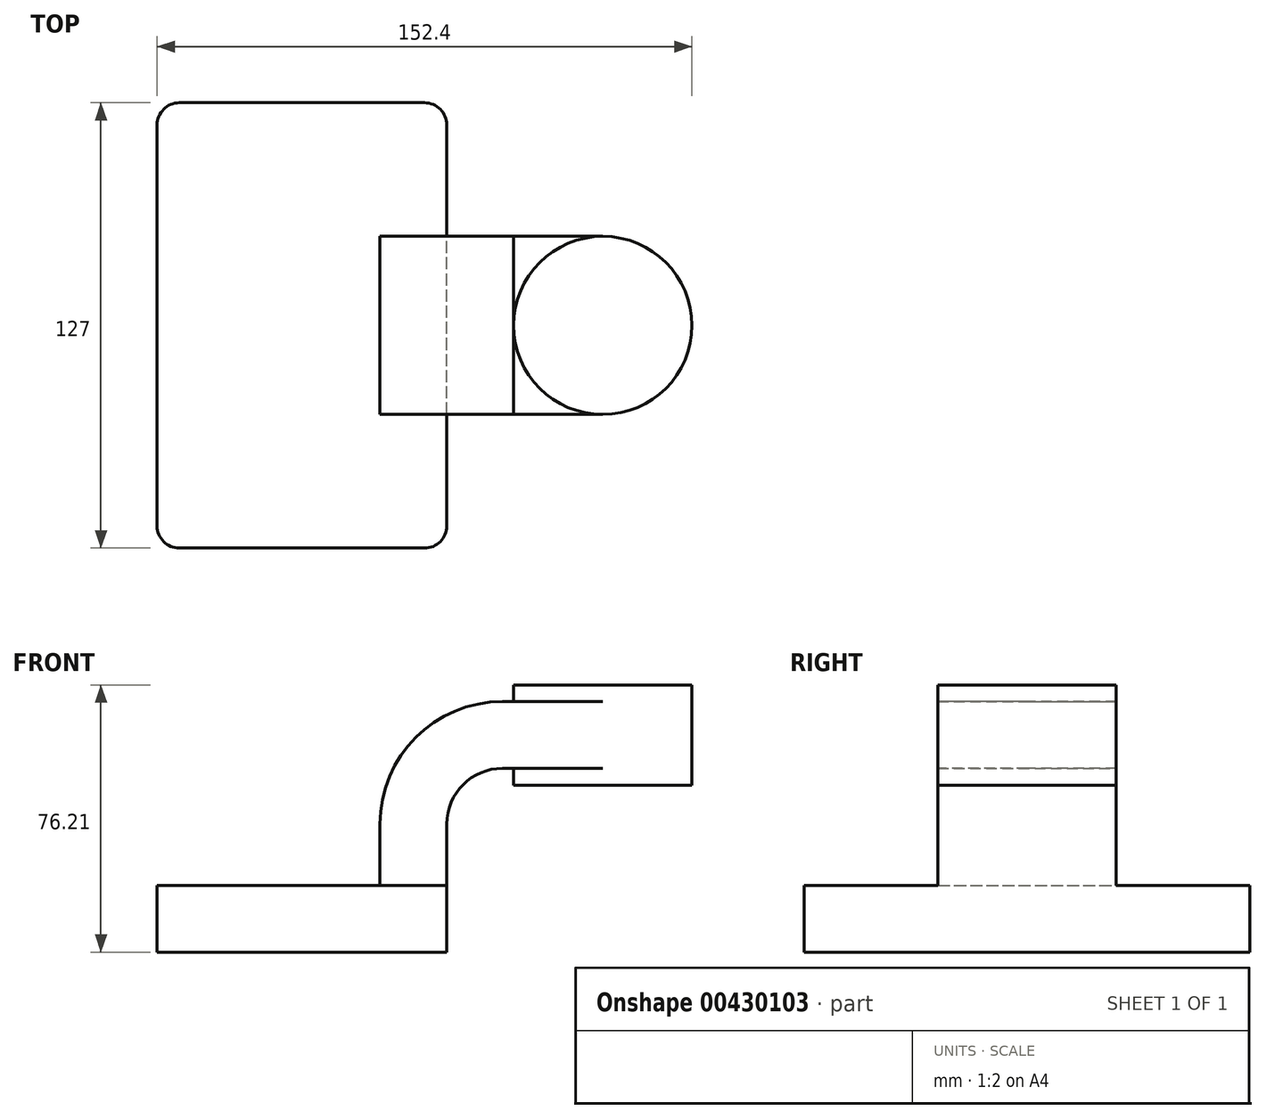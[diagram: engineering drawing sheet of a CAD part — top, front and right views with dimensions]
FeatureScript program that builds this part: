
annotation { "Feature Type Name" : "Feature", "Feature Type Description" : "" }
export const myFeature = defineFeature(function(context is Context, id is Id, definition is map)
    precondition{}
    {
        {
            var Q0;
            Q0=qCreatedBy(makeId("Front.planeOp"),FACE);
            var sketch = newSketch(context, id + "F0", { "sketchPlane" : qUnion([Q0])});
            skLineSegment(sketch, "E0.bottom", {"start": v(-41.28, -9.53) * mm, "end": v(41.28, -9.53) * mm});
            skLineSegment(sketch, "E0.top", {"start": v(-41.28, 9.53) * mm, "end": v(41.28, 9.53) * mm});
            skLineSegment(sketch, "E0.left", {"start": v(-41.28, -9.53) * mm, "end": v(-41.28, 9.53) * mm});
            skLineSegment(sketch, "E0.right", {"start": v(41.28, -9.53) * mm, "end": v(41.28, 9.53) * mm});
            skPoint(sketch, "E0.middle", {"position": v(0, 0) * mm});
            skLineSegment(sketch, "E1.bottom", {"start": v(60.32, 38.1) * mm, "end": v(111.12, 38.1) * mm});
            skLineSegment(sketch, "E1.top", {"start": v(60.32, 66.68) * mm, "end": v(111.12, 66.68) * mm});
            skLineSegment(sketch, "E1.left", {"start": v(60.32, 38.1) * mm, "end": v(60.32, 66.67) * mm});
            skLineSegment(sketch, "E1.right", {"start": v(111.12, 38.1) * mm, "end": v(111.12, 66.67) * mm});
            skPoint(sketch, "E1.middle", {"position": v(85.72, 52.39) * mm});
            skLineSegment(sketch, "E2", {"start": v(41.27, 9.53) * mm, "end": v(41.27, 27) * mm});
            skArc(sketch, "E3", {"start": v(41.27, 27) * mm, "mid": v(45.92, 38.23) * mm, "end": v(57.15, 42.88) * mm});
            skLineSegment(sketch, "E4", {"start": v(57.15, 42.88) * mm, "end": v(85.72, 42.88) * mm});
            skLineSegment(sketch, "E5.0", {"start": v(57.15, 61.93) * mm, "end": v(85.72, 61.93) * mm});
            skArc(sketch, "E5.1", {"start": v(22.22, 27) * mm, "mid": v(32.45, 51.7) * mm, "end": v(57.15, 61.93) * mm});
            skLineSegment(sketch, "E5.2", {"start": v(22.22, 9.53) * mm, "end": v(22.22, 27) * mm});
            skLineSegment(sketch, "E6", {"start": v(85.72, 38.1) * mm, "end": v(85.72, 66.68) * mm});
            skFitSpline(sketch, "E7", {"points": [v(-41.28, 9.53) * mm, v(57.15, 61.93) * mm, v(69.44, 48.53) * mm], "startDerivative": vector(110.93, 225.57) * mm, "endDerivative": vector(-272.57, -139.72) * mm});
            skSolve(sketch);
        }
        {
            var Q0;
            Q0=makeQuery(id+"F0.imprint","IMPRINT",FACE,{"disambiguationData":[TD([[makeQuery(id+"F0.imprint","IMPRINT",EDGE,{"derivedFrom":sQuery(id+"F0.wireOp",EDGE,"E0.bottom")}),1.0]])]});
            extrude(context, id + "F1", {"entities" : qUnion([Q0]), "endBound" : BoundingType.SYMMETRIC, "depth" : 127 * mm});
        }
        {
            var Q0;
            {var subQ0=sQuery(id+"F0.wireOp",EDGE,"E2");Q0=makeQuery(id+"F0.imprint","IMPRINT",FACE,{"disambiguationData":[TD([[makeQuery(id+"F0.imprint","IMPRINT",EDGE,{"derivedFrom":subQ0}),1.0]])]});}
            var Q1;
            {var subQ0=sQuery(id+"F0.wireOp",EDGE,"E4");var subQ1=sQuery(id+"F0.wireOp",EDGE,"E1.left");var subQ2=makeQuery(id+"F0.imprint","INTERSECT",VERTEX,{"derivedFrom":[subQ1,subQ0]});Q1=makeQuery(id+"F0.imprint","IMPRINT",FACE,{"disambiguationData":[TD([[makeQuery(id+"F0.imprint","IMPRINT",EDGE,{"disambiguationData":[TD([[subQ2,-1.0]])],"derivedFrom":subQ1}),-1.0]])]});}
            extrude(context, id + "F2", {"entities" : qUnion([Q0, Q1]), "operationType" : NewBodyOperationType.ADD, "endBound" : BoundingType.SYMMETRIC, "depth" : 50.8 * mm});
        }
        {
            var Q0;
            Q0=makeQuery(id+"F0.imprint","IMPRINT",FACE,{"disambiguationData":[TD([[makeQuery(id+"F0.imprint","IMPRINT",EDGE,{"derivedFrom":sQuery(id+"F0.wireOp",EDGE,"E5.1")}),1.0]])]});
            extrude(context, id + "F3", {"entities" : qUnion([Q0]), "operationType" : NewBodyOperationType.ADD, "endBound" : BoundingType.SYMMETRIC, "depth" : 15.88 * mm});
        }
        {
            var Q0;
            {var subQ0=sQuery(id+"F0.wireOp",EDGE,"E1.right");Q0=makeQuery(id+"F0.imprint","IMPRINT",FACE,{"disambiguationData":[TD([[makeQuery(id+"F0.imprint","IMPRINT",EDGE,{"derivedFrom":subQ0}),1.0]])]});}
            var Q1;
            Q1=sQuery(id+"F0.wireOp",EDGE,"E6");
            revolve(context, id + "F4", {"operationType" : NewBodyOperationType.ADD, "entities" : qUnion([Q0]), "axis" : qUnion([Q1]), "revolveType" : RevolveType.FULL});
        }
        {
            var Q0;
            Q0=makeQuery(id+"F1.opExtrude","CAP_EDGE",EDGE,{"disambiguationData":[OSD([sQuery(id+"F0.wireOp",EDGE,"E0.left")])],"isStart":false});
            var Q1;
            Q1=makeQuery(id+"F1.opExtrude","CAP_EDGE",EDGE,{"disambiguationData":[OSD([sQuery(id+"F0.wireOp",EDGE,"E0.right")])],"isStart":false});
            var Q2;
            Q2=makeQuery(id+"F1.opExtrude","CAP_EDGE",EDGE,{"disambiguationData":[OSD([sQuery(id+"F0.wireOp",EDGE,"E0.right")])],"isStart":true});
            var Q3;
            Q3=makeQuery(id+"F1.opExtrude","CAP_EDGE",EDGE,{"disambiguationData":[OSD([sQuery(id+"F0.wireOp",EDGE,"E0.left")])],"isStart":true});
            fillet(context, id + "F5", {"entities" : qUnion([Q0, Q1, Q2, Q3]), "radius" : 6.35 * mm, "tangentPropagation" : true, "allowEdgeOverflow" : false});
        }
    });
